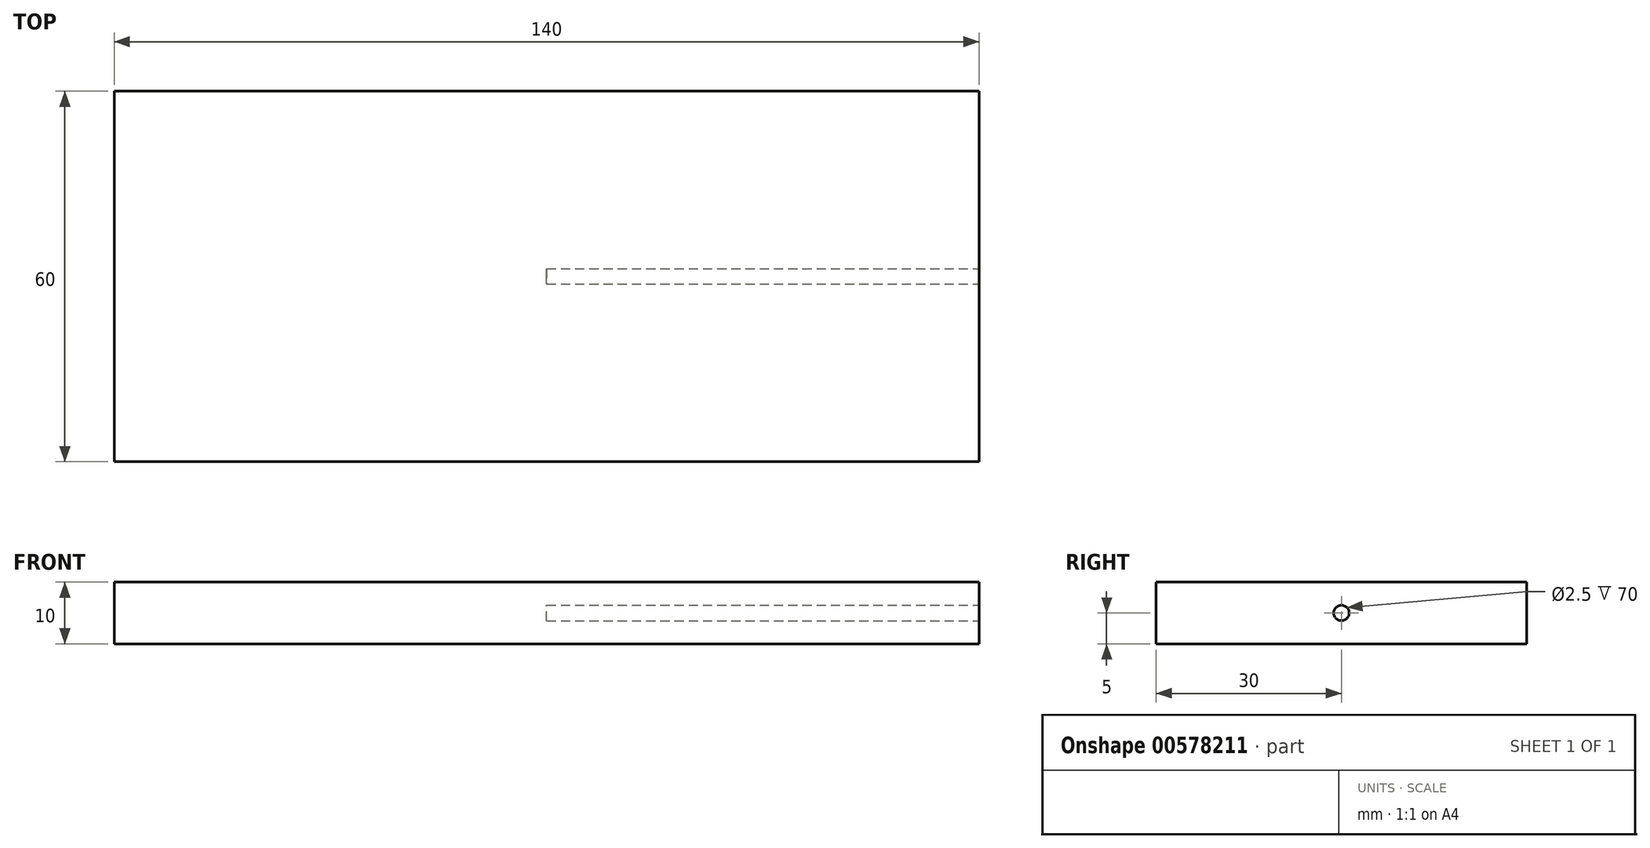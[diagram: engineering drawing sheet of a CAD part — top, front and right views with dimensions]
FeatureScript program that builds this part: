
annotation { "Feature Type Name" : "Feature", "Feature Type Description" : "" }
export const myFeature = defineFeature(function(context is Context, id is Id, definition is map)
    precondition{}
    {
        {
            var Q0;
            Q0=qCreatedBy(makeId("Top.planeOp"),FACE);
            var sketch = newSketch(context, id + "F0", { "sketchPlane" : qUnion([Q0])});
            skLineSegment(sketch, "E0.bottom", {"start": v(70, -30) * mm, "end": v(-70, -30) * mm});
            skLineSegment(sketch, "E0.top", {"start": v(70, 30) * mm, "end": v(-70, 30) * mm});
            skLineSegment(sketch, "E0.left", {"start": v(70, -30) * mm, "end": v(70, 30) * mm});
            skLineSegment(sketch, "E0.right", {"start": v(-70, -30) * mm, "end": v(-70, 30) * mm});
            skPoint(sketch, "E0.middle", {"position": v(0, 0) * mm});
            skSolve(sketch);
        }
        {
            var Q0;
            Q0 = qSketchRegion(id + "F0", true);
            extrude(context, id + "F1", {"entities" : qUnion([Q0]), "endBound" : BoundingType.SYMMETRIC, "depth" : 10 * mm, "offsetDistance" : 25 * mm});
        }
        {
            var Q0;
            Q0=makeQuery(id+"F1.opExtrude","SWEPT_FACE",FACE,{"disambiguationData":[OSD([sQuery(id+"F0.wireOp",EDGE,"E0.left")])]});
            var sketch = newSketch(context, id + "F2", { "sketchPlane" : qUnion([Q0])});
            skCircle(sketch, "E1", {"center": v(0, 0) * mm, "radius": 1.25 * mm});
            skSolve(sketch);
        }
        {
            var Q0;
            Q0 = qSketchRegion(id + "F2", true);
            extrude(context, id + "F3", {"entities" : qUnion([Q0]), "operationType" : NewBodyOperationType.REMOVE, "oppositeDirection" : true, "depth" : 70 * mm, "offsetDistance" : 25 * mm});
        }
    });
